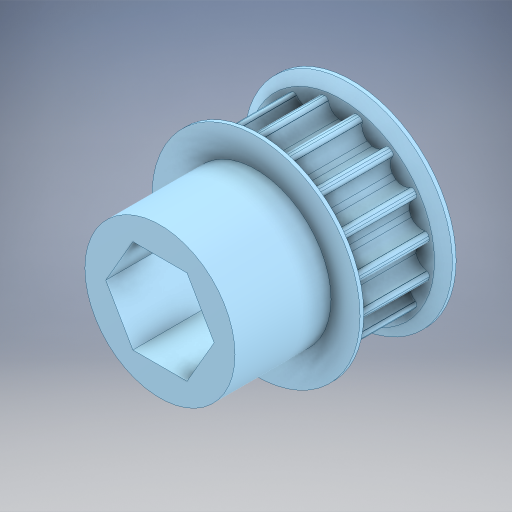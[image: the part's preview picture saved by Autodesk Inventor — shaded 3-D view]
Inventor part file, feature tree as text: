
AUTODESK INVENTOR PART (.ipt)
format: ipt  version: 2024 (Build 280153000, 153)  size: 468,480 bytes
history: native  units: in
note: dims shown in document units (in); Inventor stores cm internally (conversion verified against a paired STEP export)
features: extrude x1, sketch x1, projected_geometry x1, other x1
ambient origin geometry x8: Origin, YZ Plane, XZ Plane, XY Plane, X Axis, Y Axis, Z Axis, Center Point
bodies: Solid1 (feature_tree)
feature tree (4):
  extrude  "Extrusion1"  Depth=0.5118in TaperAngle=0.0deg
  sketch  "Sketch1"  dims[d0=0.8in d1=0.5118in d2=0.0in]
  projected_geometry  "Projected Loop1"
  other  "HTD-5mm-16T-Pulley"
